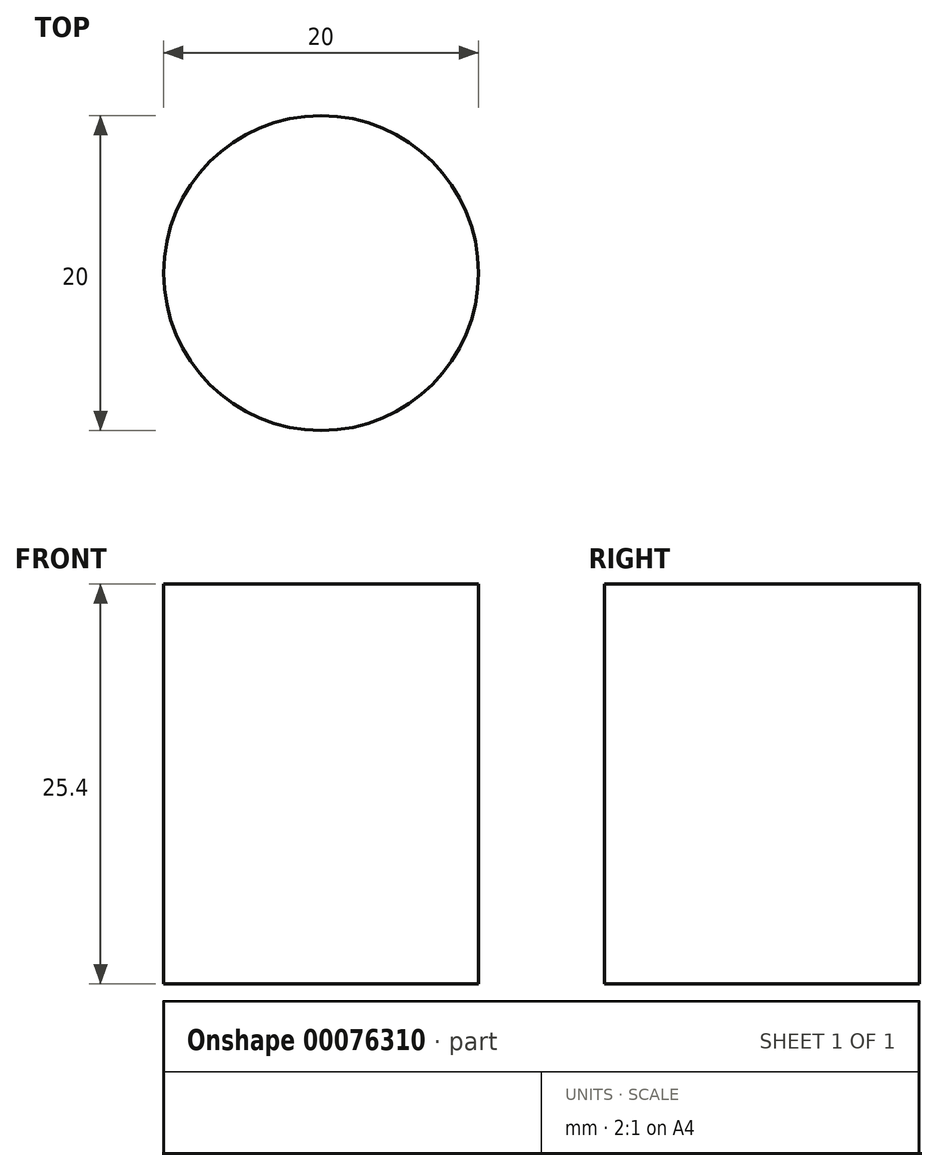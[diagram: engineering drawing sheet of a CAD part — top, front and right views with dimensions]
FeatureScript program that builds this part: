
annotation { "Feature Type Name" : "Feature", "Feature Type Description" : "" }
export const myFeature = defineFeature(function(context is Context, id is Id, definition is map)
    precondition{}
    {
        {
            var Q0;
            Q0=qCreatedBy(makeId("Top.planeOp"),FACE);
            var sketch = newSketch(context, id + "F0", { "sketchPlane" : qUnion([Q0])});
            skCircle(sketch, "E0", {"center": v(0, 0) * mm, "radius": 10 * mm});
            skSolve(sketch);
        }
        {
            var Q0;
            Q0 = qSketchRegion(id + "F0", true);
            extrude(context, id + "F1", {"entities" : qUnion([Q0]), "depth" : 25.4 * mm});
        }
    });
